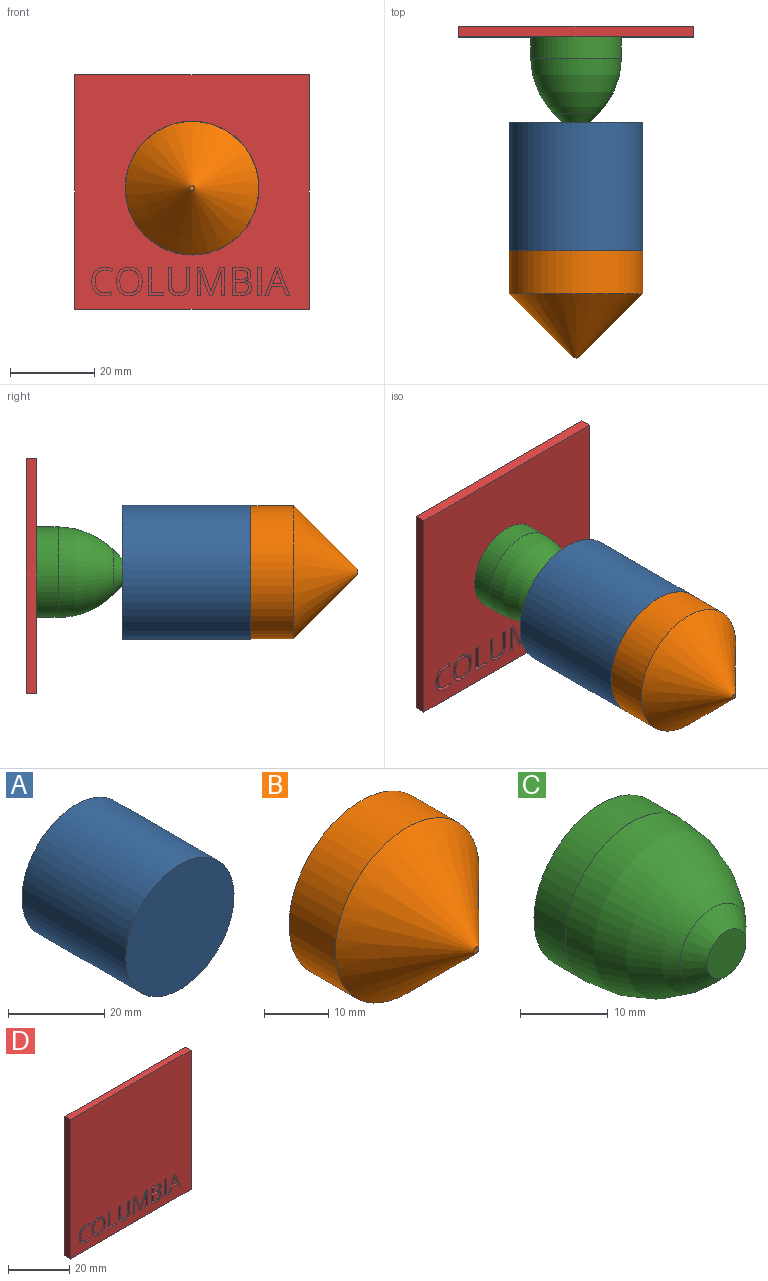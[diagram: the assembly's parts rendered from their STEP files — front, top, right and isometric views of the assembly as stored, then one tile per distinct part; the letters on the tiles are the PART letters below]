
ASSEMBLY  parts=4 mates=3
PART A: 3 faces, bbox 31.8x30.5x31.8 mm
  f0: cylinder r=15.88mm len=31.76mm, axis (0,1,0), area 3040.8mm2, adj f1,f2
  f1: plane 31.76x31.76mm, normal (0,-1,0), area 792mm2, adj f0
  f2: plane 31.76x31.76mm, normal (0,1,0), area 792mm2, adj f0
PART B: 4 faces, bbox 31.7x25.4x31.7 mm
  f0: cylinder r=15.83mm len=31.65mm, axis (0,1,0), area 1010.2mm2, adj f2,f3
  f1: plane 1.17x1.17mm, normal (0,-1,0), area 1.1mm2, adj f3
  f2: plane 31.65x31.65mm, normal (0,1,0), area 786.8mm2, adj f0
  f3: cone r=0.59mm half-angle=45deg, axis (0,1,0), area 1111.1mm2, adj f0,f1
PART C: 9 faces, bbox 21.5x20.3x21.5 mm
  f0: cylinder r=10.76mm len=21.53mm, axis (0,1,0), area 340.7mm2, adj f2,f4
  f1: plane 6.29x6.29mm, normal (0,-1,0), area 31mm2, adj f3
  f2: plane 21.53x21.53mm, normal (0,1,0), area 151.5mm2, adj f0,f5
  f3: cone r=3.14mm half-angle=45deg, axis (0,1,0), area 83.1mm2, adj f1,f4
  f4: revolved ~21.53x21.53mm, area 1628.3mm2, adj f0,f3
  f5: cylinder r=8.22mm len=16.45mm, axis (0,1,0), area 260.3mm2, adj f2,f8
  f6: plane 4.18x4.18mm, normal (0,1,0), area 13.7mm2, adj f7
  f7: cone r=1.35mm half-angle=45deg, axis (0,1,0), area 36.5mm2, adj f6,f8
  f8: revolved ~16.45x16.45mm, area 1044.5mm2, adj f5,f7
PART D: 129 faces, bbox 55.6x2.5x55.6 mm
  f0: plane 55.57x55.57mm, normal (0,-1,0), area 2959.8mm2, adj f1,f2,f3,f4,f6,f7,f8,f9
  f1: plane 55.57x2.54mm, normal (0,0,1), area 141.1mm2, adj f0,f2,f4,f5
  f2: plane 55.57x2.54mm, normal (-1,0,0), area 141.1mm2, adj f0,f1,f3,f5
  f3: plane 55.57x2.54mm, normal (0,0,-1), area 141.1mm2, adj f0,f2,f4,f5
  f4: plane 55.57x2.54mm, normal (1,0,0), area 141.1mm2, adj f0,f1,f3,f5
  f5: plane 55.57x55.57mm, normal (0,1,0), area 3087.8mm2, adj f1,f2,f3,f4
  f6: plane 6.63x1.27mm, normal (1,0,0), area 8.4mm2, adj f0,f7,f11,f12
  f7: plane 3.69x1.27mm, normal (0,0,1), area 4.7mm2, adj f0,f6,f8,f12
  f8: plane 1.27x0.7mm, normal (-1,0,0), area 0.9mm2, adj f0,f7,f9,f12
  f9: plane 2.92x1.27mm, normal (0,0,-1), area 3.7mm2, adj f0,f8,f10,f12
  f10: plane 5.93x1.27mm, normal (-1,0,0), area 7.5mm2, adj f0,f9,f11,f12
  f11: plane 1.27x0.77mm, normal (0,0,-1), area 1mm2, adj f0,f6,f10,f12
  f12: plane 6.63x3.69mm, normal (0,-1,0), area 7.1mm2, adj f6,f7,f8,f9,f10,f11
  f13: plane 4.29x1.27mm, normal (-1,0,0), area 5.4mm2, adj f0,f14,f26,f27
  f14: plane 1.27x0.77mm, normal (0,0,-1), area 1mm2, adj f0,f13,f15,f27
  f15: plane 4.32x1.27mm, normal (1,0,0), area 5.5mm2, adj f0,f14,f16,f27
  f16: extruded ~1.28x1.27mm, area 1.8mm2, adj f0,f15,f17,f27
  f17: extruded ~1.29x1.27mm, area 1.8mm2, adj f0,f16,f18,f27
  f18: extruded ~1.33x1.27mm, area 1.8mm2, adj f0,f17,f19,f27
  f19: extruded ~1.27x1.27mm, area 1.8mm2, adj f0,f18,f20,f27
  f20: plane 4.32x1.27mm, normal (-1,0,0), area 5.5mm2, adj f0,f19,f21,f27
  f21: plane 1.27x0.77mm, normal (0,0,-1), area 1mm2, adj f0,f20,f22,f27
  f22: plane 4.27x1.27mm, normal (1,0,0), area 5.4mm2, adj f0,f21,f23,f27
  f23: extruded ~1.8x1.27mm, area 2.5mm2, adj f0,f22,f24,f27
  f24: extruded ~1.85x1.27mm, area 2.6mm2, adj f0,f23,f25,f27
  f25: extruded ~1.88x1.27mm, area 2.6mm2, adj f0,f24,f26,f27
  f26: extruded ~1.78x1.27mm, area 2.5mm2, adj f0,f13,f25,f27
  f27: plane 6.72x5.07mm, normal (0,-1,0), area 11.5mm2, adj f13,f14,f15,f16,f17,f18,f19,f20
  f28: plane 5.87x2.25mm, normal (0.93,0,0.36), area 8mm2, adj f0,f29,f45,f46
  f29: plane 1.27x0.62mm, normal (0,0,1), area 0.8mm2, adj f0,f28,f30,f46
  f30: plane 5.87x2.27mm, normal (-0.93,0,0.36), area 8mm2, adj f0,f29,f31,f46
  f31: plane 1.27x0.04mm, normal (0,0,1), area 0mm2, adj f0,f30,f32,f46
  f32: extruded ~1.6x1.27mm, area 2mm2, adj f0,f31,f33,f46
  f33: plane 4.27x1.27mm, normal (1,0,0), area 5.4mm2, adj f0,f32,f34,f46
  f34: plane 1.27x0.77mm, normal (0,0,1), area 1mm2, adj f0,f33,f35,f46
  f35: plane 6.63x1.27mm, normal (-1,0,0), area 8.4mm2, adj f0,f34,f36,f46
  f36: plane 1.27x1.15mm, normal (0,0,-1), area 1.5mm2, adj f0,f35,f37,f46
  f37: plane 5.47x2.12mm, normal (0.93,0,-0.36), area 7.4mm2, adj f0,f36,f38,f46
  f38: plane 1.27x0.04mm, normal (0,0,-1), area 0mm2, adj f0,f37,f39,f46
  f39: plane 5.47x2.1mm, normal (-0.93,0,-0.36), area 7.4mm2, adj f0,f38,f40,f46
  f40: plane 1.27x1.16mm, normal (0,0,-1), area 1.5mm2, adj f0,f39,f41,f46
  f41: plane 6.63x1.27mm, normal (1,0,0), area 8.4mm2, adj f0,f40,f42,f46
  f42: plane 1.27x0.71mm, normal (0,0,1), area 0.9mm2, adj f0,f41,f43,f46
  f43: plane 4.22x1.27mm, normal (-1,0,0), area 5.4mm2, adj f0,f42,f44,f46
  f44: extruded ~1.66x1.27mm, area 2.1mm2, adj f0,f43,f45,f46
  f45: plane 1.27x0.04mm, normal (0,0,1), area 0mm2, adj f0,f28,f44,f46
  f46: plane 6.63x6.56mm, normal (0,-1,0), area 18.8mm2, adj f28,f29,f30,f31,f32,f33,f34,f35
  f47: plane 6.63x1.27mm, normal (1,0,0), area 8.4mm2, adj f0,f48,f50,f51
  f48: plane 1.27x0.77mm, normal (0,0,1), area 1mm2, adj f0,f47,f49,f51
  f49: plane 6.63x1.27mm, normal (-1,0,0), area 8.4mm2, adj f0,f48,f50,f51
  f50: plane 1.27x0.77mm, normal (0,0,-1), area 1mm2, adj f0,f47,f49,f51
  f51: plane 6.63x0.77mm, normal (0,-1,0), area 5.1mm2, adj f47,f48,f49,f50
  f52: plane 2.48x1.27mm, normal (-1,0,0), area 3.1mm2, adj f53,f76,f77,f126
  f53: plane 1.32x1.27mm, normal (0,0,1), area 1.7mm2, adj f52,f54,f77,f126
  f54: extruded ~1.27x1.26mm, area 1.7mm2, adj f53,f55,f77,f126
  f55: extruded ~1.27x0.91mm, area 1.3mm2, adj f54,f56,f77,f126
  f56: extruded ~1.27x0.97mm, area 1.4mm2, adj f55,f57,f77,f126
  f57: extruded ~1.27x1.21mm, area 1.6mm2, adj f56,f76,f77,f126
  f58: plane 1.27x1.27mm, normal (0,0,-1), area 1.6mm2, adj f59,f74,f77,f78
  f59: plane 2.17x1.27mm, normal (-1,0,0), area 2.8mm2, adj f58,f60,f77,f78
  f60: plane 1.27x1.13mm, normal (0,0,1), area 1.4mm2, adj f59,f61,f77,f78
  f61: extruded ~1.27x1.27mm, area 1.7mm2, adj f60,f62,f77,f78
  f62: extruded ~1.27x0.81mm, area 1.2mm2, adj f61,f63,f77,f78
  f63: extruded ~1.27x0.86mm, area 1.2mm2, adj f62,f74,f77,f78
  f64: plane 1.87x1.27mm, normal (0,0,-1), area 2.4mm2, adj f0,f65,f75,f77
  f65: plane 6.63x1.27mm, normal (1,0,0), area 8.4mm2, adj f0,f64,f66,f77
  f66: plane 2.31x1.27mm, normal (0,0,1), area 2.9mm2, adj f0,f65,f67,f77
  f67: extruded ~1.68x1.27mm, area 2.3mm2, adj f0,f66,f68,f77
  f68: extruded ~1.39x1.27mm, area 2mm2, adj f0,f67,f69,f77
  f69: extruded ~1.59x1.51mm, area 3.1mm2, adj f0,f68,f70,f77
  f70: plane 1.27x0.05mm, normal (-1,0,0), area 0.1mm2, adj f0,f69,f71,f77
  f71: extruded ~1.27x0.96mm, area 1.4mm2, adj f0,f70,f72,f77
  f72: extruded ~1.27x0.97mm, area 1.3mm2, adj f0,f71,f73,f77
  f73: extruded ~1.27x1.25mm, area 1.8mm2, adj f0,f72,f75,f77
  f74: extruded ~1.27x1.18mm, area 1.5mm2, adj f58,f63,f77,f78
  f75: extruded ~1.91x1.27mm, area 2.5mm2, adj f0,f64,f73,f77
  f76: plane 1.38x1.27mm, normal (0,0,-1), area 1.8mm2, adj f52,f57,f77,f126
  f77: plane 6.63x4.59mm, normal (0,-1,0), area 15mm2, adj f52,f53,f54,f55,f56,f57,f58,f59
  f78: plane 2.8x2.17mm, normal (0,-1,0), area 5.6mm2, adj f58,f59,f60,f61,f62,f63,f74
  f79: plane 2.05x1.27mm, normal (0.94,0,0.35), area 2.8mm2, adj f80,f91,f92,f127
  f80: plane 2.14x1.27mm, normal (0,0,-1), area 2.7mm2, adj f79,f81,f92,f127
  f81: plane 2.05x1.27mm, normal (-0.94,0,0.35), area 2.8mm2, adj f80,f82,f92,f127
  f82: extruded ~1.27x0.96mm, area 1.3mm2, adj f81,f91,f92,f127
  f83: plane 2.11x1.27mm, normal (0.93,0,0.36), area 2.9mm2, adj f0,f84,f90,f92
  f84: plane 1.27x0.8mm, normal (0,0,1), area 1mm2, adj f0,f83,f85,f92
  f85: plane 6.65x2.61mm, normal (-0.93,0,-0.36), area 9.1mm2, adj f0,f84,f86,f92
  f86: plane 1.27x0.65mm, normal (0,0,-1), area 0.8mm2, adj f0,f85,f87,f92
  f87: plane 6.65x2.62mm, normal (0.93,0,-0.37), area 9.1mm2, adj f0,f86,f88,f92
  f88: plane 1.27x0.78mm, normal (0,0,1), area 1mm2, adj f0,f87,f89,f92
  f89: plane 2.11x1.27mm, normal (-0.93,0,0.36), area 2.9mm2, adj f0,f88,f90,f92
  f90: plane 2.66x1.27mm, normal (0,0,1), area 3.4mm2, adj f0,f83,f89,f92
  f91: extruded ~1.27x0.96mm, area 1.3mm2, adj f79,f82,f92,f127
  f92: plane 6.65x5.87mm, normal (0,-1,0), area 11.3mm2, adj f79,f80,f81,f82,f83,f84,f85,f86
  f93: extruded ~2.04x1.27mm, area 2.7mm2, adj f94,f108,f109,f128
  f94: extruded ~2.02x1.27mm, area 2.7mm2, adj f93,f95,f109,f128
  f95: extruded ~1.67x1.27mm, area 2.4mm2, adj f94,f96,f109,f128
  f96: extruded ~1.66x1.27mm, area 2.4mm2, adj f95,f97,f109,f128
  f97: extruded ~2.03x1.27mm, area 2.7mm2, adj f96,f98,f109,f128
  f98: extruded ~2.05x1.27mm, area 2.7mm2, adj f97,f99,f109,f128
  f99: extruded ~1.66x1.27mm, area 2.4mm2, adj f98,f108,f109,f128
  f100: extruded ~2.5x1.27mm, area 3.4mm2, adj f0,f101,f107,f109
  f101: extruded ~2.5x1.27mm, area 3.4mm2, adj f0,f100,f102,f109
  f102: extruded ~2.23x1.27mm, area 3.2mm2, adj f0,f101,f103,f109
  f103: extruded ~2.27x1.27mm, area 3.2mm2, adj f0,f102,f104,f109
  f104: extruded ~2.51x1.27mm, area 3.4mm2, adj f0,f103,f105,f109
  f105: extruded ~2.53x1.27mm, area 3.4mm2, adj f0,f104,f106,f109
  f106: extruded ~2.26x1.27mm, area 3.2mm2, adj f0,f105,f107,f109
  f107: extruded ~2.24x1.27mm, area 3.2mm2, adj f0,f100,f106,f109
  f108: extruded ~1.67x1.27mm, area 2.4mm2, adj f93,f99,f109,f128
  f109: plane 6.82x6.1mm, normal (0,-1,0), area 13.9mm2, adj f93,f94,f95,f96,f97,f98,f99,f100
  f110: extruded ~1.72x1.27mm, area 2.5mm2, adj f0,f111,f124,f125
  f111: extruded ~1.51x1.27mm, area 2mm2, adj f0,f110,f112,f125
  f112: plane 1.27x0.66mm, normal (-0.9,0,0.44), area 0.9mm2, adj f0,f111,f113,f125
  f113: extruded ~1.82x1.27mm, area 2.4mm2, adj f0,f112,f114,f125
  f114: extruded ~1.7x1.27mm, area 2.3mm2, adj f0,f113,f115,f125
  f115: extruded ~1.27x1.19mm, area 2.1mm2, adj f0,f114,f116,f125
  f116: extruded ~1.79x1.27mm, area 2.4mm2, adj f0,f115,f117,f125
  f117: extruded ~2.53x1.27mm, area 3.4mm2, adj f0,f116,f118,f125
  f118: extruded ~2.26x1.27mm, area 3.2mm2, adj f0,f117,f119,f125
  f119: extruded ~1.7x1.27mm, area 2.2mm2, adj f0,f118,f120,f125
  f120: plane 1.27x0.67mm, normal (-1,0,0), area 0.9mm2, adj f0,f119,f121,f125
  f121: extruded ~1.58x1.27mm, area 2mm2, adj f0,f120,f122,f125
  f122: extruded ~1.74x1.27mm, area 2.5mm2, adj f0,f121,f123,f125
  f123: extruded ~2.01x1.27mm, area 2.7mm2, adj f0,f122,f124,f125
  f124: extruded ~1.99x1.27mm, area 2.7mm2, adj f0,f110,f123,f125
  f125: plane 6.81x5.01mm, normal (0,-1,0), area 9.6mm2, adj f110,f111,f112,f113,f114,f115,f116,f117
  f126: plane 3x2.48mm, normal (0,-1,0), area 6.8mm2, adj f52,f53,f54,f55,f56,f57,f76
  f127: plane 3.01x2.14mm, normal (0,-1,0), area 3.1mm2, adj f79,f80,f81,f82,f91
  f128: plane 5.46x4.46mm, normal (0,-1,0), area 20.2mm2, adj f93,f94,f95,f96,f97,f98,f99,f108
PLACE A t=(48.82,-42.3,-60.65)mm
PLACE B t=(-32.71,-72.78,-62.75)mm
PLACE C t=(49.97,-21.98,8.86)mm
PLACE D t=(-30.53,-19.44,22.16)mm
MATE fastened B.f0 <-> A.f0  axis (0,1,0) through (7.67,-72.78,-21.6)mm
MATE fastened C.f0 <-> D.f0  axis (0,1,0) through (7.67,-21.98,-21.6)mm
MATE fastened A.f0 <-> C.f0  axis (0,1,0) through (7.67,-42.3,-21.6)mm
